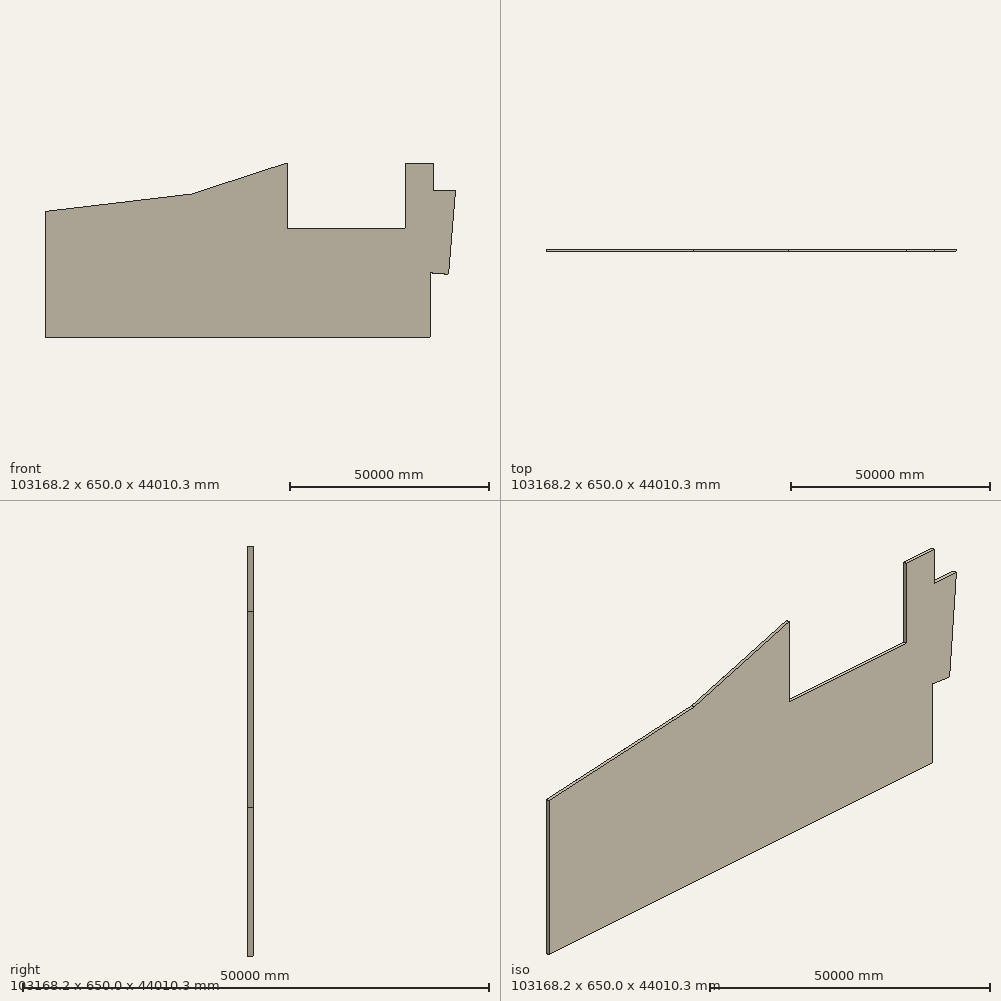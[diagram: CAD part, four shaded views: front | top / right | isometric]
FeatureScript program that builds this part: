
annotation { "Feature Type Name" : "Feature", "Feature Type Description" : "" }
export const myFeature = defineFeature(function(context is Context, id is Id, definition is map)
    precondition{}
    {
        {
            var Q0;
            Q0=qCreatedBy(makeId("Front.planeOp"),FACE);
            var sketch = newSketch(context, id + "F0", { "sketchPlane" : qUnion([Q0])});
            skLineSegment(sketch, "E0", {"start": v(0, 31823) * mm, "end": v(0, 0) * mm});
            skLineSegment(sketch, "E1", {"start": v(0, 0) * mm, "end": v(96994, 0) * mm});
            skLineSegment(sketch, "E2", {"start": v(0, 31823) * mm, "end": v(36871, 36212.16) * mm});
            skLineSegment(sketch, "E3", {"start": v(36871, 36212.16) * mm, "end": v(60811, 44010.33) * mm});
            skLineSegment(sketch, "E4", {"start": v(96994, 0) * mm, "end": v(96994, 16380) * mm});
            skPoint(sketch, "E5.end.orphan", {"position": v(65379, 52169.09) * mm});
            skPoint(sketch, "E6.end.orphan", {"position": v(91413.67, 52169.09) * mm});
            skLineSegment(sketch, "E7", {"start": v(60811, 44010.33) * mm, "end": v(60811, 27425.33) * mm});
            skLineSegment(sketch, "E8", {"start": v(60811, 27425.33) * mm, "end": v(90501, 27425.33) * mm});
            skLineSegment(sketch, "E9", {"start": v(96994, 16380) * mm, "end": v(101428, 16012.2) * mm});
            skLineSegment(sketch, "E10", {"start": v(101428, 16012.2) * mm, "end": v(103168.2, 36991.2) * mm});
            skLineSegment(sketch, "E11", {"start": v(90501, 27425.33) * mm, "end": v(90501, 44010.33) * mm});
            skLineSegment(sketch, "E12", {"start": v(90501, 44010.33) * mm, "end": v(97573.88, 44010.33) * mm});
            skLineSegment(sketch, "E13", {"start": v(97573.88, 44010.33) * mm, "end": v(97573.88, 36991.2) * mm});
            skLineSegment(sketch, "E14", {"start": v(97573.88, 36991.2) * mm, "end": v(103168.2, 36991.2) * mm});
            skSolve(sketch);
        }
        {
            var Q0;
            Q0=qSketchRegion(id+"F0",true);
            extrude(context, id + "F1", {"entities" : qUnion([Q0]), "depth" : 650 * mm});
        }
    });
